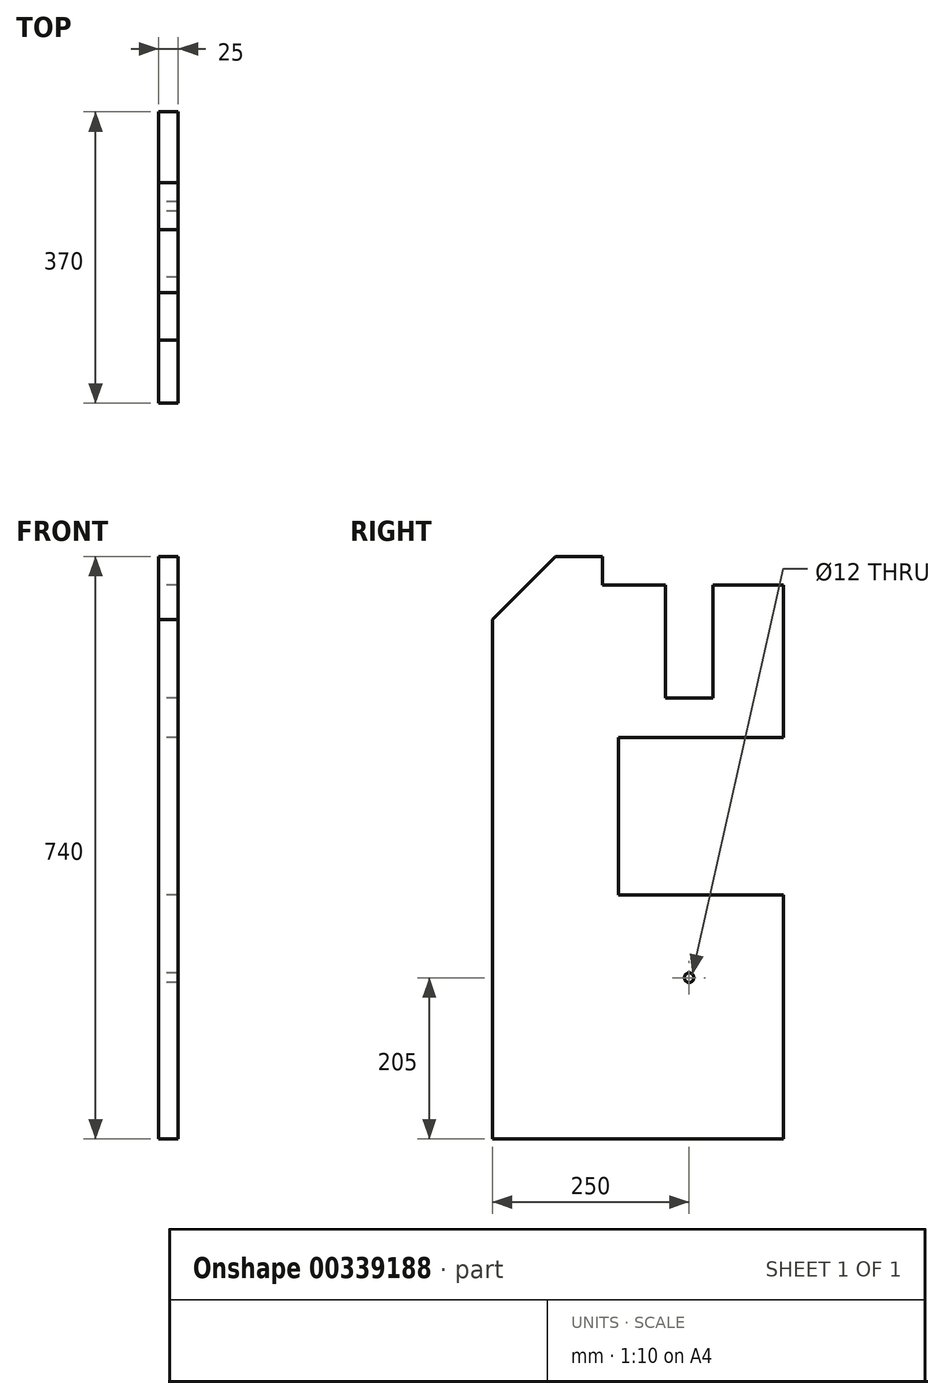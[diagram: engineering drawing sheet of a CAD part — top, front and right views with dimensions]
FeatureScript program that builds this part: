
annotation { "Feature Type Name" : "Feature", "Feature Type Description" : "" }
export const myFeature = defineFeature(function(context is Context, id is Id, definition is map)
    precondition{}
    {
        {
            var Q0;
            Q0=qCreatedBy(makeId("Right.planeOp"),FACE);
            var sketch = newSketch(context, id + "F0", { "sketchPlane" : qUnion([Q0])});
            skLineSegment(sketch, "E0", {"start": v(0, 0) * mm, "end": v(0, 740) * mm});
            skLineSegment(sketch, "E1", {"start": v(0, 740) * mm, "end": v(140, 740) * mm});
            skLineSegment(sketch, "E2", {"start": v(370, 704) * mm, "end": v(370, 510) * mm});
            skLineSegment(sketch, "E3", {"start": v(0, 0) * mm, "end": v(370, 0) * mm});
            skLineSegment(sketch, "E4", {"start": v(370, 0) * mm, "end": v(370, 310) * mm});
            skLineSegment(sketch, "E5", {"start": v(370, 310) * mm, "end": v(160, 310) * mm});
            skLineSegment(sketch, "E6", {"start": v(160, 310) * mm, "end": v(160, 510) * mm});
            skLineSegment(sketch, "E7", {"start": v(160, 510) * mm, "end": v(370, 510) * mm});
            skCircle(sketch, "E8", {"center": v(250, 205) * mm, "radius": 6 * mm});
            skLineSegment(sketch, "E9.top", {"start": v(220, 560) * mm, "end": v(280, 560) * mm});
            skLineSegment(sketch, "E9.left", {"start": v(220, 704) * mm, "end": v(220, 560) * mm});
            skLineSegment(sketch, "E9.right", {"start": v(280, 704) * mm, "end": v(280, 560) * mm});
            skLineSegment(sketch, "E10", {"start": v(370, 704) * mm, "end": v(280, 704) * mm});
            skLineSegment(sketch, "E11", {"start": v(140, 704) * mm, "end": v(140, 740) * mm});
            skLineSegment(sketch, "E12.trimOffspring", {"start": v(220, 704) * mm, "end": v(140, 704) * mm});
            skPoint(sketch, "E13.orphan", {"position": v(370, 740) * mm});
            skSolve(sketch);
        }
        {
            var Q0;
            Q0=makeQuery(id+"F0.imprint","IMPRINT",FACE,{"disambiguationData":[TD([[makeQuery(id+"F0.imprint","IMPRINT",EDGE,{"derivedFrom":sQuery(id+"F0.wireOp",EDGE,"E0")}),-1.0]])]});
            extrude(context, id + "F1", {"entities" : qUnion([Q0]), "depth" : 25 * mm});
        }
        {
            var Q0;
            Q0=makeQuery(id+"F1.opExtrude","SWEPT_EDGE",EDGE,{"disambiguationData":[OSD([sQuery(id+"F0.wireOp",EDGE,"E0"),sQuery(id+"F0.wireOp",EDGE,"E1")])]});
            chamfer(context, id + "F2", {"entities" : qUnion([Q0]), "width" : 80 * mm, "tangentPropagation" : true});
        }
    });
